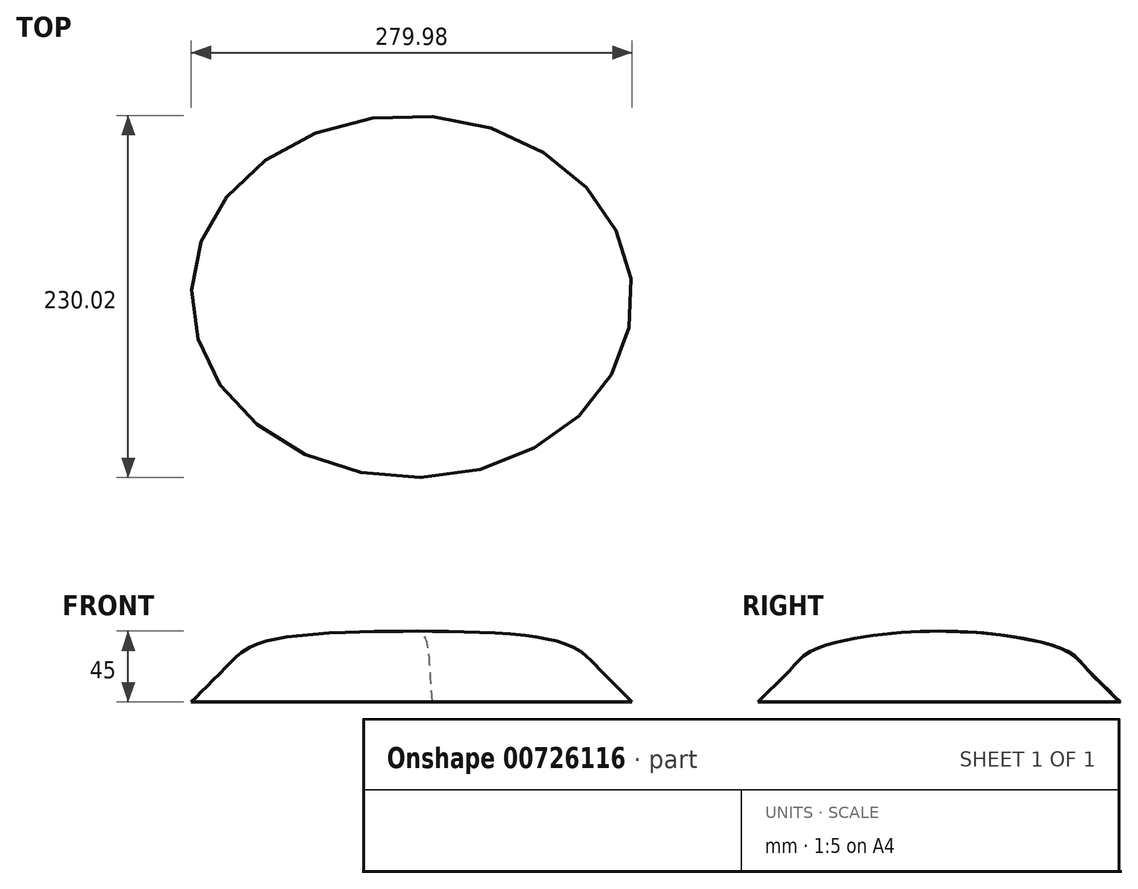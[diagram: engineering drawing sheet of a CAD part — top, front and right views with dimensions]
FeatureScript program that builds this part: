
annotation { "Feature Type Name" : "Feature", "Feature Type Description" : "" }
export const myFeature = defineFeature(function(context is Context, id is Id, definition is map)
    precondition{}
    {
        {
            var Q0;
            Q0=qCreatedBy(makeId("Top.planeOp"),FACE);
            cPlane(context, id + "F0", {"entities" : qUnion([Q0]), "cplaneType" : CPlaneType.OFFSET, "offset" : 10 * mm, "width" : 152.4 * mm, "height" : 152.4 * mm});
        }
        {
            var Q0;
            Q0=qCreatedBy(makeId("Top.planeOp"),FACE);
            cPlane(context, id + "F1", {"entities" : qUnion([Q0]), "cplaneType" : CPlaneType.OFFSET, "offset" : 20 * mm, "width" : 150 * mm, "height" : 150 * mm});
        }
        {
            var Q0;
            Q0=qCreatedBy(makeId("Top.planeOp"),FACE);
            cPlane(context, id + "F2", {"entities" : qUnion([Q0]), "cplaneType" : CPlaneType.OFFSET, "offset" : 30 * mm, "width" : 150 * mm, "height" : 150 * mm});
        }
        {
            var Q0;
            Q0=qCreatedBy(makeId("Top.planeOp"),FACE);
            cPlane(context, id + "F3", {"entities" : qUnion([Q0]), "cplaneType" : CPlaneType.OFFSET, "offset" : 40 * mm, "width" : 150 * mm, "height" : 150 * mm});
        }
        {
            var Q0;
            Q0=qCreatedBy(makeId("Top.planeOp"),FACE);
            var sketch = newSketch(context, id + "F4", { "sketchPlane" : qUnion([Q0])});
            skLineSegment(sketch, "E0", {"start": v(-194.13, 0) * mm, "end": v(177.94, 0) * mm, "construction": true});
            skEllipse(sketch, "E1", {"center": v(0, 0) * mm, "majorRadius": 140 * mm, "minorRadius": 115 * mm, "majorAxis": v(-1, 0.02)});
            skSolve(sketch);
        }
        {
            var Q0;
            Q0=qCreatedBy(id+"F0.planeOp",FACE);
            var sketch = newSketch(context, id + "F5", { "sketchPlane" : qUnion([Q0])});
            skEllipse(sketch, "E2", {"center": v(0, 0) * mm, "majorRadius": 130 * mm, "minorRadius": 105 * mm, "majorAxis": v(-1, 0)});
            skSolve(sketch);
        }
        {
            var Q0;
            Q0=qCreatedBy(id+"F1.planeOp",FACE);
            var sketch = newSketch(context, id + "F6", { "sketchPlane" : qUnion([Q0])});
            skEllipse(sketch, "E3", {"center": v(0, 0) * mm, "majorRadius": 120 * mm, "minorRadius": 95 * mm, "majorAxis": v(-1, 0)});
            skSolve(sketch);
        }
        {
            var Q0;
            Q0=qCreatedBy(id+"F2.planeOp",FACE);
            var sketch = newSketch(context, id + "F7", { "sketchPlane" : qUnion([Q0])});
            skEllipse(sketch, "E4", {"center": v(0, 0) * mm, "majorRadius": 110 * mm, "minorRadius": 85 * mm, "majorAxis": v(-1, 0)});
            skSolve(sketch);
        }
        {
            var Q0;
            Q0=qCreatedBy(id+"F3.planeOp",FACE);
            var sketch = newSketch(context, id + "F8", { "sketchPlane" : qUnion([Q0])});
            skEllipse(sketch, "E5", {"center": v(0, 0) * mm, "majorRadius": 86.33 * mm, "minorRadius": 55.59 * mm, "majorAxis": v(-1, 0)});
            skSolve(sketch);
        }
        {
            var Q0;
            Q0=qCreatedBy(makeId("Top.planeOp"),FACE);
            cPlane(context, id + "F9", {"entities" : qUnion([Q0]), "cplaneType" : CPlaneType.OFFSET, "offset" : 45 * mm, "width" : 150 * mm, "height" : 150 * mm});
        }
        {
            var Q0;
            Q0=qCreatedBy(id+"F9.planeOp",FACE);
            var sketch = newSketch(context, id + "F10", { "sketchPlane" : qUnion([Q0])});
            skCircle(sketch, "E6", {"center": v(3.5, 0) * mm, "radius": 2.01 * mm});
            skSolve(sketch);
        }
        {
            var Q0;
            Q0=sQuery(id+"F4.wireOp",EDGE,"E1");
            var Q1;
            Q1=sQuery(id+"F5.wireOp",EDGE,"E2");
            var Q2;
            Q2=sQuery(id+"F6.wireOp",EDGE,"E3");
            var Q3;
            Q3=sQuery(id+"F7.wireOp",EDGE,"E4");
            var Q4;
            Q4=sQuery(id+"F8.wireOp",EDGE,"E5");
            var Q5;
            Q5=sQuery(id+"F10.wireOp",VERTEX,"E6.center");
            loft(context, id + "F11", {"bodyType" : ToolBodyType.SURFACE, "wireProfilesArray" : [{ "wireProfileEntities" : qUnion([Q0]) }, { "wireProfileEntities" : qUnion([Q1]) }, { "wireProfileEntities" : qUnion([Q2]) }, { "wireProfileEntities" : qUnion([Q3]) }, { "wireProfileEntities" : qUnion([Q4]) }, { "wireProfileEntities" : qUnion([Q5]) }]});
        }
    });
